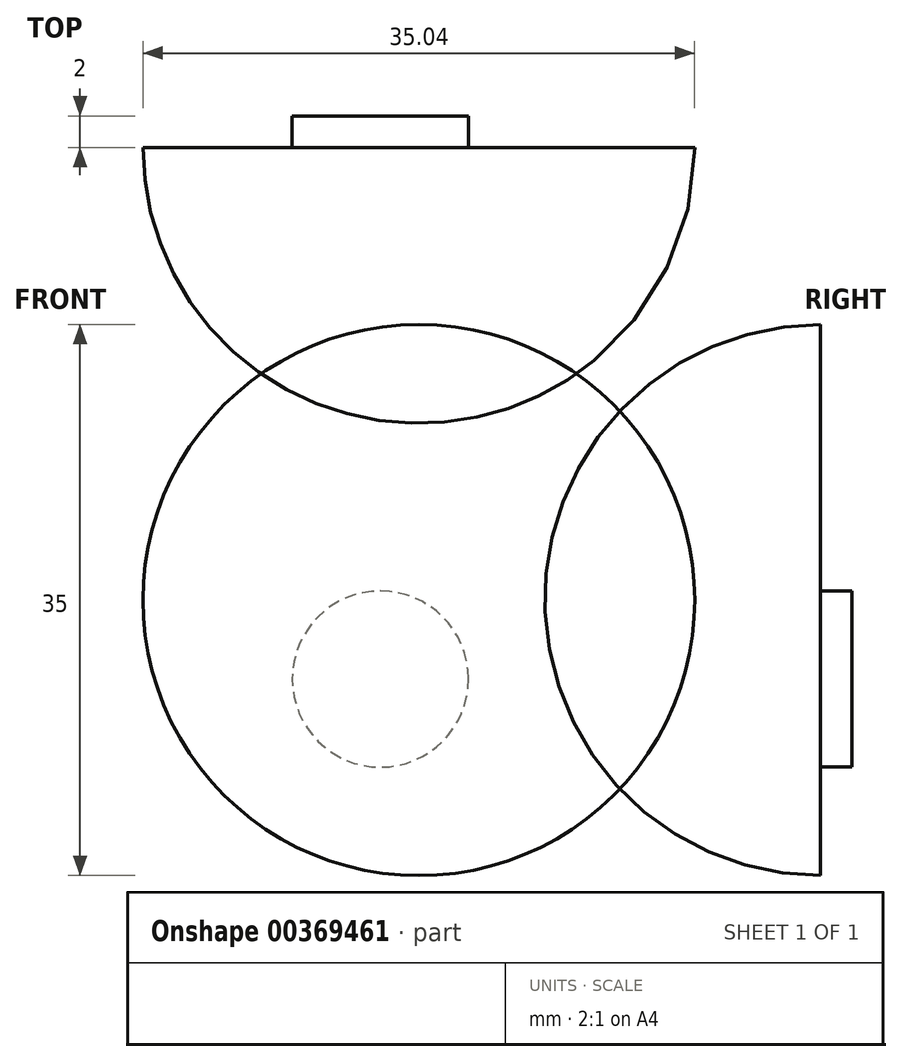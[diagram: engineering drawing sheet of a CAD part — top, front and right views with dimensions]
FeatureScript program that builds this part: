
annotation { "Feature Type Name" : "Feature", "Feature Type Description" : "" }
export const myFeature = defineFeature(function(context is Context, id is Id, definition is map)
    precondition{}
    {
        {
            var Q0;
            Q0=qCreatedBy(makeId("Front.planeOp"),FACE);
            var sketch = newSketch(context, id + "F0", { "sketchPlane" : qUnion([Q0])});
            skLineSegment(sketch, "E0", {"start": v(0, 0) * mm, "end": v(0, 35) * mm});
            skArc(sketch, "E1", {"start": v(0, 35) * mm, "mid": v(-17.52, 17.5) * mm, "end": v(0, 0) * mm});
            skSolve(sketch);
        }
        {
            var Q0;
            Q0=makeQuery(id+"F0.imprint","IMPRINT",FACE,{"disambiguationData":[TD([[makeQuery(id+"F0.imprint","IMPRINT",EDGE,{"derivedFrom":sQuery(id+"F0.wireOp",EDGE,"E0")}),1.0]])]});
            var Q1;
            Q1=sQuery(id+"F0.wireOp",EDGE,"E0");
            revolve(context, id + "F1", {"entities" : qUnion([Q0]), "axis" : qUnion([Q1]), "revolveType" : RevolveType.ONE_DIRECTION, "angle" : 180 * degree});
        }
        {
            var Q0;
            Q0=makeQuery(id+"F1.opRevolve","CAP_FACE",FACE,{"disambiguationData":[OSD([sQuery(id+"F0.wireOp",EDGE,"E0"),sQuery(id+"F0.wireOp",EDGE,"E1")])],"isStart":false});
            var sketch = newSketch(context, id + "F2", { "sketchPlane" : qUnion([Q0])});
            skCircle(sketch, "E2", {"center": v(2.45, 12.48) * mm, "radius": 5.6 * mm});
            skPoint(sketch, "E2.first.point", {"position": v(4.66, 17.62) * mm});
            skPoint(sketch, "E2.second.point", {"position": v(-0.02, 17.5) * mm});
            skPoint(sketch, "E2.third.point", {"position": v(-3, 13.79) * mm});
            skSolve(sketch);
        }
        {
            var Q0;
            Q0=makeQuery(id+"F2.imprint","IMPRINT",FACE,{"disambiguationData":[TD([[makeQuery(id+"F2.imprint","IMPRINT",EDGE,{"derivedFrom":sQuery(id+"F2.wireOp",EDGE,"E2")}),1.0]])]});
            extrude(context, id + "F3", {"entities" : qUnion([Q0]), "operationType" : NewBodyOperationType.ADD, "depth" : 2 * mm, "offsetDistance" : 25 * mm});
        }
    });
